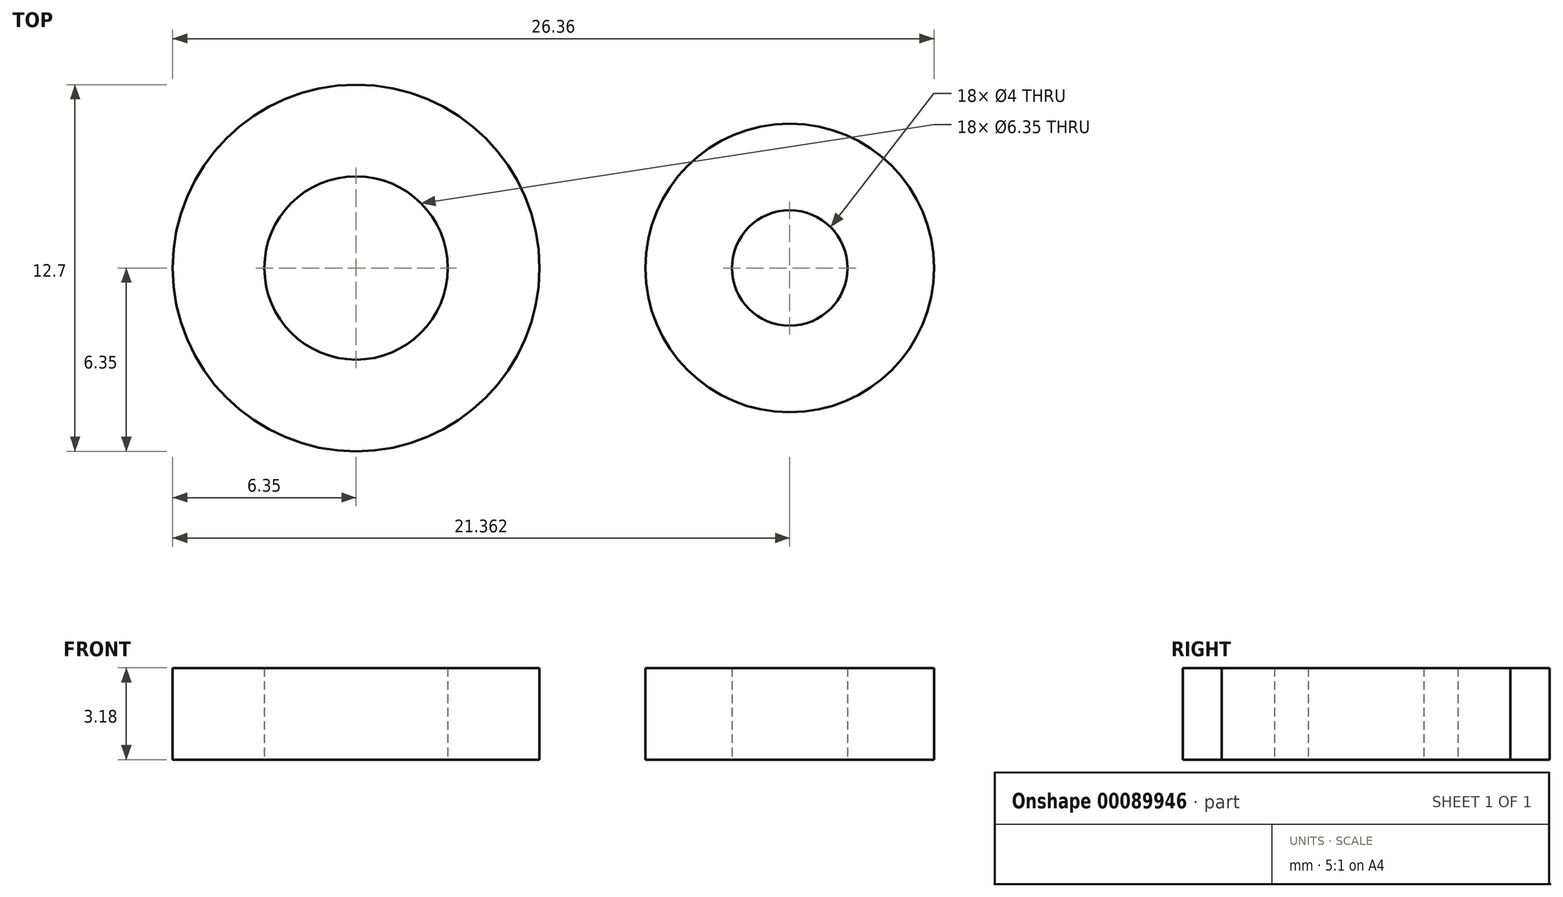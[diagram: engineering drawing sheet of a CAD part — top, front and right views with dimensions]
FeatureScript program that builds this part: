
annotation { "Feature Type Name" : "Feature", "Feature Type Description" : "" }
export const myFeature = defineFeature(function(context is Context, id is Id, definition is map)
    precondition{}
    {
        {
            var Q0;
            Q0=qCreatedBy(makeId("Top.planeOp"),FACE);
            var sketch = newSketch(context, id + "F0", { "sketchPlane" : qUnion([Q0])});
            skCircle(sketch, "E0", {"center": v(0, 0) * mm, "radius": 6.35 * mm});
            skCircle(sketch, "E1", {"center": v(0, 0) * mm, "radius": 3.18 * mm});
            skSolve(sketch);
        }
        {
            var Q0;
            Q0 = qSketchRegion(id + "F0", true);
            extrude(context, id + "F1", {"entities" : qUnion([Q0]), "depth" : 3.17 * mm});
        }
        {
            var Q0;
            Q0=qCreatedBy(makeId("Top.planeOp"),FACE);
            var sketch = newSketch(context, id + "F2", { "sketchPlane" : qUnion([Q0])});
            skCircle(sketch, "E2", {"center": v(15.01, 0) * mm, "radius": 5 * mm});
            skCircle(sketch, "E3", {"center": v(15.01, 0) * mm, "radius": 2 * mm});
            skSolve(sketch);
        }
        {
            var Q0;
            Q0=makeQuery(id+"F2.imprint","IMPRINT",FACE,{"disambiguationData":[TD([[makeQuery(id+"F2.imprint","IMPRINT",EDGE,{"derivedFrom":sQuery(id+"F2.wireOp",EDGE,"E2")}),1.0]])]});
            extrude(context, id + "F3", {"entities" : qUnion([Q0]), "depth" : 3.17 * mm});
        }
    });
